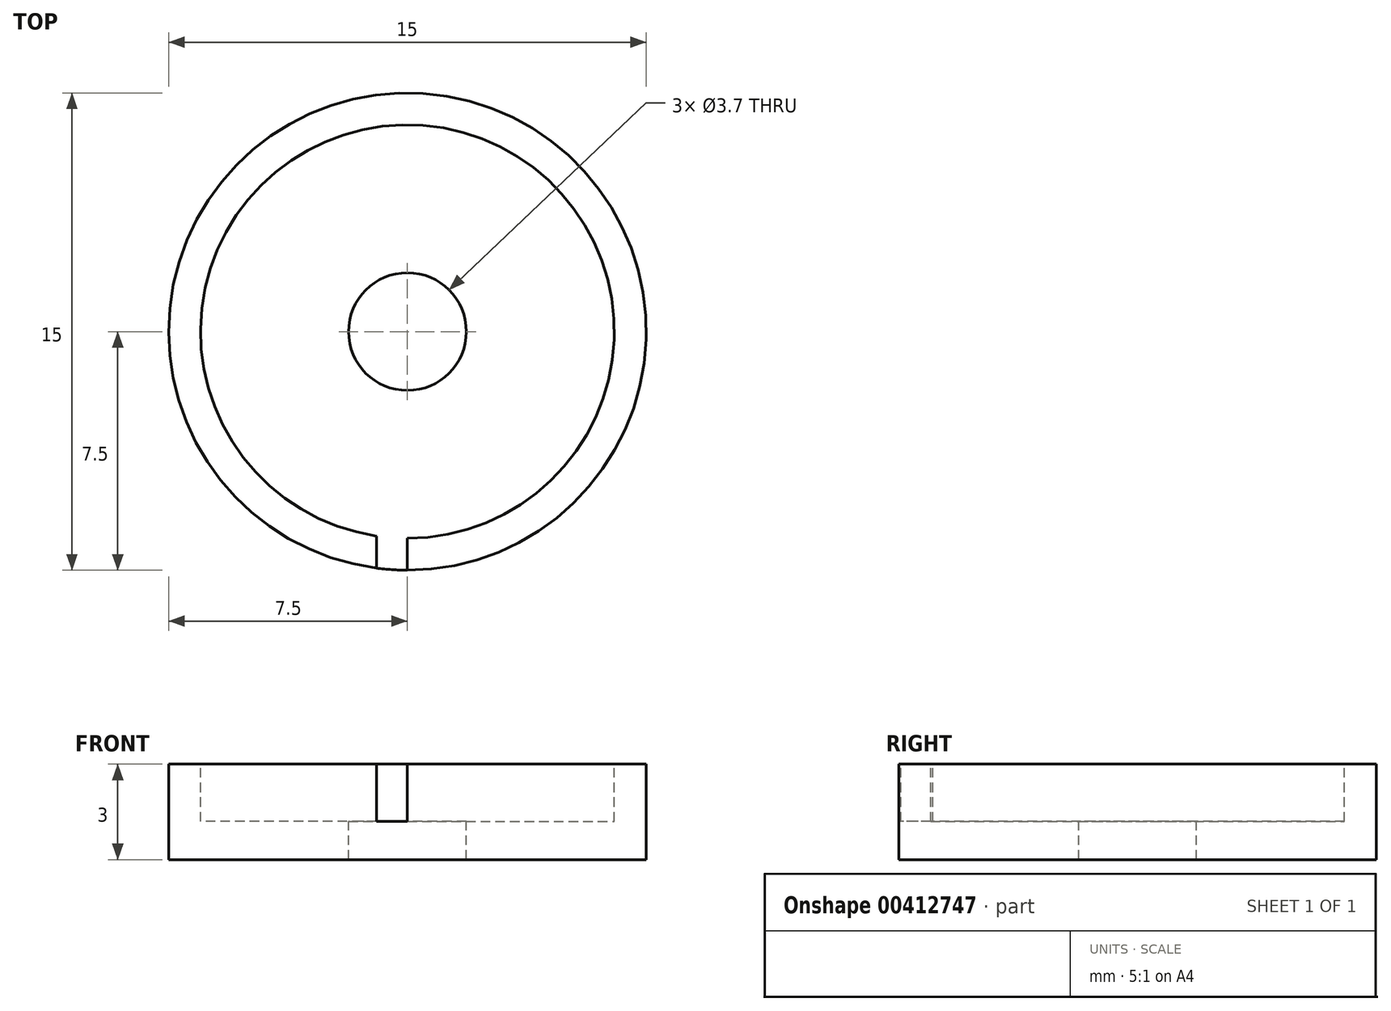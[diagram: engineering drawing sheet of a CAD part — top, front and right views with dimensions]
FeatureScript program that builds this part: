
annotation { "Feature Type Name" : "Feature", "Feature Type Description" : "" }
export const myFeature = defineFeature(function(context is Context, id is Id, definition is map)
    precondition{}
    {
        {
            var Q0;
            Q0=qCreatedBy(makeId("Top.planeOp"),FACE);
            var sketch = newSketch(context, id + "F0", { "sketchPlane" : qUnion([Q0])});
            skCircle(sketch, "E0", {"center": v(0, 0) * mm, "radius": 7.5 * mm});
            skSolve(sketch);
        }
        {
            var Q0;
            Q0 = qSketchRegion(id + "F0", true);
            extrude(context, id + "F1", {"entities" : qUnion([Q0]), "depth" : 3 * mm});
        }
        {
            var Q0;
            Q0=makeQuery(id+"F1.opExtrude","CAP_FACE",FACE,{"disambiguationData":[OSD([sQuery(id+"F0.wireOp",EDGE,"E0")])],"isStart":false});
            var sketch = newSketch(context, id + "F2", { "sketchPlane" : qUnion([Q0])});
            skCircle(sketch, "E1.0", {"center": v(0, 0) * mm, "radius": 6.5 * mm});
            skSolve(sketch);
        }
        {
            var Q0;
            Q0=makeQuery(id+"F2.imprint","IMPRINT",FACE,{"disambiguationData":[TD([[makeQuery(id+"F2.imprint","IMPRINT",EDGE,{"derivedFrom":sQuery(id+"F2.wireOp",EDGE,"E1.0")}),1.0]])]});
            extrude(context, id + "F3", {"entities" : qUnion([Q0]), "operationType" : NewBodyOperationType.REMOVE, "oppositeDirection" : true, "depth" : 1.8 * mm});
        }
        {
            var Q0;
            Q0=makeQuery(id+"F1.opExtrude","CAP_FACE",FACE,{"disambiguationData":[OSD([sQuery(id+"F0.wireOp",EDGE,"E0")])],"isStart":false});
            var sketch = newSketch(context, id + "F4", { "sketchPlane" : qUnion([Q0])});
            skLineSegment(sketch, "E2", {"start": v(0, -6.5) * mm, "end": v(0, -7.5) * mm});
            skLineSegment(sketch, "E3", {"start": v(-0.98, -6.43) * mm, "end": v(-0.98, -7.44) * mm});
            skSolve(sketch);
        }
        {
            var Q0;
            Q0 = qSketchRegion(id + "F4", true);
            var Q1;
            {var subQ0=sQuery(id+"F4.wireOp",EDGE,"E2");Q1=makeQuery(id+"F4.imprint","IMPRINT",FACE,{"disambiguationData":[TD([[makeQuery(id+"F4.imprint","IMPRINT",EDGE,{"derivedFrom":subQ0}),-1.0]])]});}
            extrude(context, id + "F5", {"entities" : qUnion([Q0, Q1]), "operationType" : NewBodyOperationType.REMOVE, "oppositeDirection" : true, "depth" : 1.8 * mm});
        }
        {
            var Q0;
            {var subQ0=sQuery(id+"F2.wireOp",EDGE,"E1.0");Q0=makeQuery(id+"F5.boolean.opBoolean","MERGE",FACE,{"derivedFrom":[makeQuery(id+"F3.boolean.opBoolean","COPY",FACE,{"derivedFrom":makeQuery(id+"F3.opExtrude","CAP_FACE",FACE,{"disambiguationData":[OSD([subQ0])],"isStart":false})}),makeQuery(id+"F5.opExtrude","CAP_FACE",FACE,{"disambiguationData":[OSD([sQuery(id+"F0.wireOp",EDGE,"E0"),subQ0,sQuery(id+"F4.wireOp",EDGE,"E2"),sQuery(id+"F4.wireOp",EDGE,"E3")])],"isStart":false})]});}
            var sketch = newSketch(context, id + "F6", { "sketchPlane" : qUnion([Q0])});
            skCircle(sketch, "E4", {"center": v(0, 0) * mm, "radius": 1.85 * mm});
            skSolve(sketch);
        }
        {
            var Q0;
            Q0=makeQuery(id+"F6.imprint","IMPRINT",FACE,{"disambiguationData":[TD([[makeQuery(id+"F6.imprint","IMPRINT",EDGE,{"derivedFrom":sQuery(id+"F6.wireOp",EDGE,"E4")}),1.0]])]});
            extrude(context, id + "F7", {"entities" : qUnion([Q0]), "operationType" : NewBodyOperationType.REMOVE, "depth" : -2 * mm});
        }
    });
